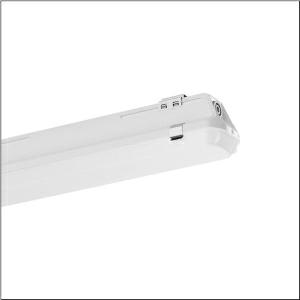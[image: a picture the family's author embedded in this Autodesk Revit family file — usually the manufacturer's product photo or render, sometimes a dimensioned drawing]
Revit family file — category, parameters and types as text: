
# Revit family: monsun_r__21_51fb10ml460j_9ac7
name_source: partatom
category: Lighting Fixtures
units: mm (PartAtom-declared; Revit-internal decimal feet)

## family parameters
Cut with Voids When Loaded = No
Host = Face
Light Source = No
Part Type = Normal
Room Calculation Point = No
Round Connector Dimension = Use Diameter
Shared = No

## types (1)
- --- (1 x LED, 3890 lm, 23.2 W, 4000K)
    Apparent Load = 23 VA
    CIE Flux Codes = 46 76 93 94 100
    Color Rendering = 80
    Color Temperature = 4000K
    Default Elevation = 1800 mm
    Description = Monsun® 21, damp-proof luminaire, chain hanger, primary optical cover: enclosure, of PMMA, light emission: direct distribution, primary light characteristic: symmetric, installation type: suspended mounting, surface-mounted, horizontal mounting, vertical mounting, LED, rated luminous flux: 6.010lm, luminous efficacy: 162lm/W, light colour: 840, colour temperature: 4000K, control gear: ECG, with terminal, 3-pole, max. 2.5mm², mains connection: 220..240V, AC, 50/60Hz, rated input power: 37W, housing, of glass-fibre reinforced plastic, uncoated, bright grey, incl. chain hanger, length: 1.299mm, width: 90mm, height: 88mm, clip for enclosure, of stainless steel (V2A), ceiling mounting element, of stainless steel (V2A), chain hanger, of stainless steel (V2A), protection rating (complete): IP66, insulation class (complete): insulation class I (protective earthing), certification: CE, ENEC, VDE, UKCA, protection symbol: D, impact resistance: IK04, permissible operating ambient temperature: -25..+35°C, standard: EN 50419, EN 60598-2-1, corresponds to IFS (International Featured Standards) requirements for safety and quality in the food industry, for indoor or canopied outdoor use, no direct snow, no direct sun, no direct rain, contact your sales advisor before using the luminaires in applications with unclear chemical exposure, large temperature fluctuations or condensation-forming humidity, LABS conformity tested according to VDMA 24364:2018-05, packaging unit: 1 piece
    Height = 88 mm
    Lamp = 1 x LED
    Lamp Light Flux = 3890 lm
    Lamp Power = 23.2 W
    Lamp count = 1
    Length = 1299 mm
    Luminous efficacy = 168 lm/W
    Manufacturer = Siteco
    ModVariant = No
    Model = 51FB10ML460J
    Mounting Place = Ceiling
    Mounting Type = Surface mounted
    Number of Poles = 1
    OnlyDefault = Yes
    Power Factor = 1
    Product Name = Monsun® 21
    Product group = damp-proof luminaire
    ProductGroupID = 300
    Protection Class = Protection class I
    Protection Degree = IP 66
    RLX_Detail_Level = 1
    RLX_Emergency_Light_Flux = 0 lm
    RLX_Emergency_Type = 0
    RLX_Emergency_Type_DB = No
    RlxData = <blob elided: 91125 chars, md5=427ac69d>
    Socket = socket
    Standby Power = 0 W
    System Light Flux = 3890 lm
    System Power = 23 W
    Type Comments = factory setting: luminous flux: 65 % | (A | C | E) | 53 mA
    Type Image = l_1006717.jpg
    URL = http://relux.com
    VarID = @adj_078091
    Voltage = 0 V
    Weight = 0.00 kg
    Width = 90 mm

## geometry (parser evidence)
native form markers: Blend x4, Sweep x11
no freeform markers — native parametric forms only
